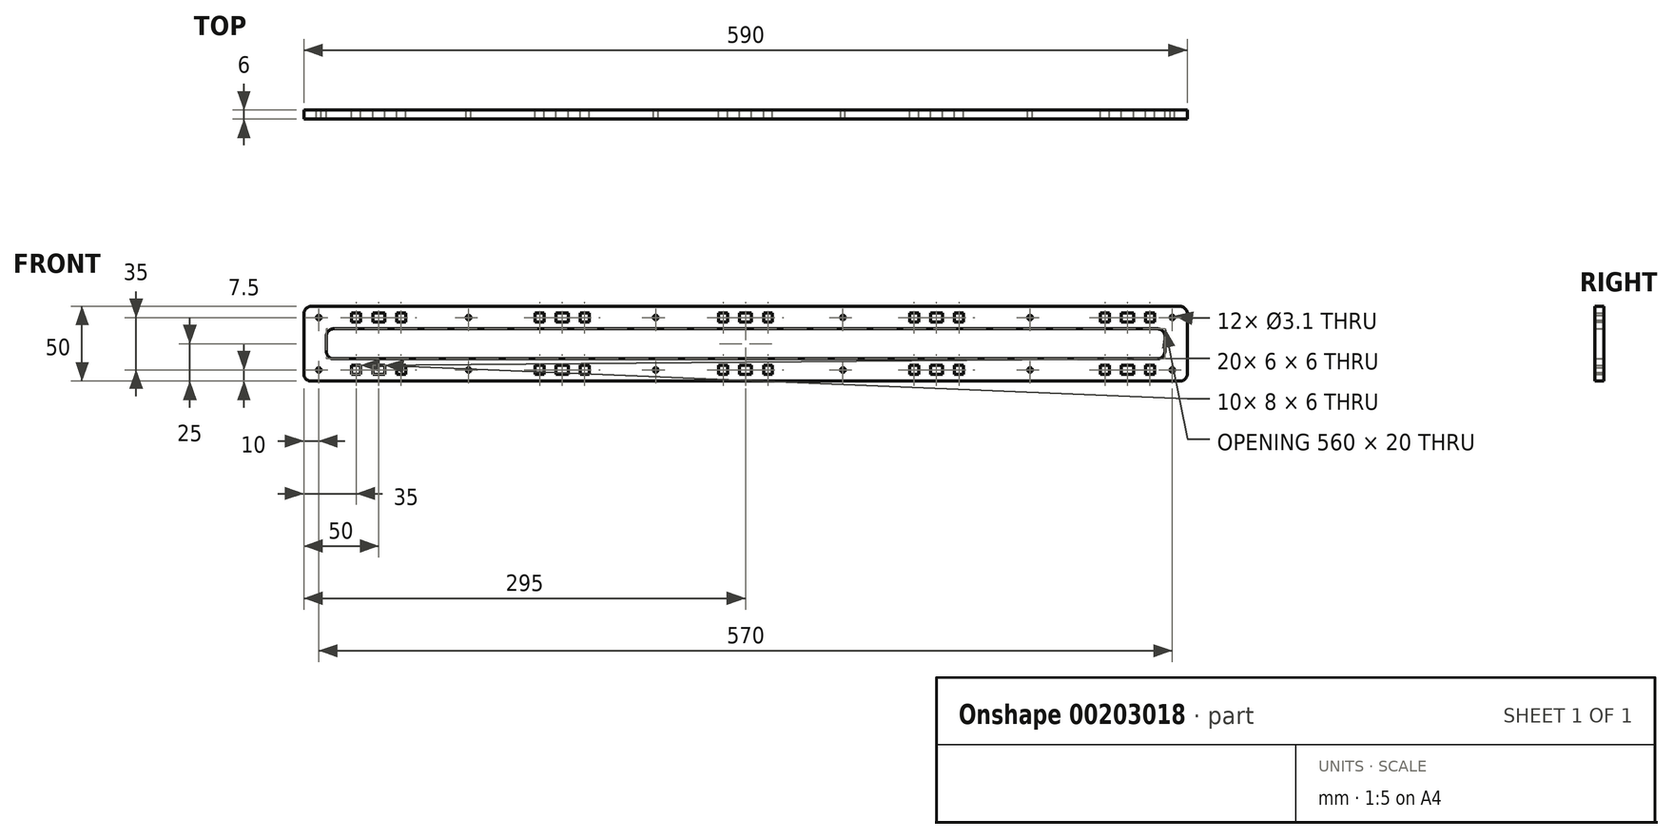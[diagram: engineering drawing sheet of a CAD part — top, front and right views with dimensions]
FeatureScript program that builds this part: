
annotation { "Feature Type Name" : "Feature", "Feature Type Description" : "" }
export const myFeature = defineFeature(function(context is Context, id is Id, definition is map)
    precondition{}
    {
        {
            var Q0;
            Q0=qCreatedBy(makeId("Front.planeOp"),FACE);
            var sketch = newSketch(context, id + "F0", { "sketchPlane" : qUnion([Q0])});
            skLineSegment(sketch, "E0", {"start": v(-290, 33.16) * mm, "end": v(290, 33.16) * mm});
            skArc(sketch, "E1", {"start": v(290, 33.16) * mm, "mid": v(293.54, 31.7) * mm, "end": v(295, 28.16) * mm});
            skLineSegment(sketch, "E2", {"start": v(295, 28.16) * mm, "end": v(295, -11.84) * mm});
            skArc(sketch, "E3", {"start": v(295, -11.84) * mm, "mid": v(293.54, -15.38) * mm, "end": v(290, -16.84) * mm});
            skLineSegment(sketch, "E4", {"start": v(290, -16.84) * mm, "end": v(-290, -16.84) * mm});
            skArc(sketch, "E5", {"start": v(-290, -16.84) * mm, "mid": v(-293.54, -15.38) * mm, "end": v(-295, -11.84) * mm});
            skLineSegment(sketch, "E6", {"start": v(-295, -11.84) * mm, "end": v(-295, 28.16) * mm});
            skArc(sketch, "E7", {"start": v(-295, 28.16) * mm, "mid": v(-293.54, 31.7) * mm, "end": v(-290, 33.16) * mm});
            skCircle(sketch, "E8", {"center": v(-285, -9.34) * mm, "radius": 1.55 * mm});
            skCircle(sketch, "E9", {"center": v(-285, 25.66) * mm, "radius": 1.55 * mm});
            skCircle(sketch, "E10", {"center": v(285, -9.34) * mm, "radius": 1.55 * mm});
            skCircle(sketch, "E11", {"center": v(285, 25.66) * mm, "radius": 1.55 * mm});
            skLineSegment(sketch, "E12", {"start": v(-275, 18.16) * mm, "end": v(275, 18.16) * mm});
            skArc(sketch, "E13", {"start": v(275, 18.16) * mm, "mid": v(278.54, 16.7) * mm, "end": v(280, 13.16) * mm});
            skLineSegment(sketch, "E14", {"start": v(280, 13.16) * mm, "end": v(280, 3.16) * mm});
            skArc(sketch, "E15", {"start": v(280, 3.16) * mm, "mid": v(278.54, -0.38) * mm, "end": v(275, -1.84) * mm});
            skLineSegment(sketch, "E16", {"start": v(275, -1.84) * mm, "end": v(-275, -1.84) * mm});
            skArc(sketch, "E17", {"start": v(-275, -1.84) * mm, "mid": v(-278.54, -0.38) * mm, "end": v(-280, 3.16) * mm});
            skLineSegment(sketch, "E18", {"start": v(-280, 3.16) * mm, "end": v(-280, 13.16) * mm});
            skArc(sketch, "E19", {"start": v(-280, 13.16) * mm, "mid": v(-278.54, 16.7) * mm, "end": v(-275, 18.16) * mm});
            skLineSegment(sketch, "E20", {"start": v(-249, 22.66) * mm, "end": v(-249, 28.66) * mm});
            skLineSegment(sketch, "E21", {"start": v(-249, 28.66) * mm, "end": v(-241, 28.66) * mm});
            skLineSegment(sketch, "E22", {"start": v(-241, 28.66) * mm, "end": v(-241, 22.66) * mm});
            skLineSegment(sketch, "E23", {"start": v(-241, 22.66) * mm, "end": v(-249, 22.66) * mm});
            skLineSegment(sketch, "E24", {"start": v(-233, 22.66) * mm, "end": v(-233, 28.66) * mm});
            skLineSegment(sketch, "E25", {"start": v(-233, 28.66) * mm, "end": v(-227, 28.66) * mm});
            skLineSegment(sketch, "E26", {"start": v(-227, 28.66) * mm, "end": v(-227, 22.66) * mm});
            skLineSegment(sketch, "E27", {"start": v(-227, 22.66) * mm, "end": v(-233, 22.66) * mm});
            skLineSegment(sketch, "E28", {"start": v(-257, 22.66) * mm, "end": v(-257, 28.66) * mm});
            skLineSegment(sketch, "E29", {"start": v(-257, 28.66) * mm, "end": v(-263, 28.66) * mm});
            skLineSegment(sketch, "E30", {"start": v(-263, 28.66) * mm, "end": v(-263, 22.66) * mm});
            skLineSegment(sketch, "E31", {"start": v(-263, 22.66) * mm, "end": v(-257, 22.66) * mm});
            skLineSegment(sketch, "E32", {"start": v(-126.5, 22.62) * mm, "end": v(-126.5, 28.62) * mm});
            skLineSegment(sketch, "E33", {"start": v(-126.5, 28.62) * mm, "end": v(-118.5, 28.62) * mm});
            skLineSegment(sketch, "E34", {"start": v(-118.5, 28.62) * mm, "end": v(-118.5, 22.62) * mm});
            skLineSegment(sketch, "E35", {"start": v(-118.5, 22.62) * mm, "end": v(-126.5, 22.62) * mm});
            skLineSegment(sketch, "E36", {"start": v(-110.5, 22.62) * mm, "end": v(-110.5, 28.62) * mm});
            skLineSegment(sketch, "E37", {"start": v(-110.5, 28.62) * mm, "end": v(-104.5, 28.62) * mm});
            skLineSegment(sketch, "E38", {"start": v(-104.5, 28.62) * mm, "end": v(-104.5, 22.62) * mm});
            skLineSegment(sketch, "E39", {"start": v(-104.5, 22.62) * mm, "end": v(-110.5, 22.62) * mm});
            skLineSegment(sketch, "E40", {"start": v(-134.5, 22.62) * mm, "end": v(-134.5, 28.62) * mm});
            skLineSegment(sketch, "E41", {"start": v(-134.5, 28.62) * mm, "end": v(-140.5, 28.62) * mm});
            skLineSegment(sketch, "E42", {"start": v(-140.5, 28.62) * mm, "end": v(-140.5, 22.62) * mm});
            skLineSegment(sketch, "E43", {"start": v(-140.5, 22.62) * mm, "end": v(-134.5, 22.62) * mm});
            skLineSegment(sketch, "E44", {"start": v(-4, 22.59) * mm, "end": v(-4, 28.59) * mm});
            skLineSegment(sketch, "E45", {"start": v(-4, 28.59) * mm, "end": v(4, 28.59) * mm});
            skLineSegment(sketch, "E46", {"start": v(4, 28.59) * mm, "end": v(4, 22.59) * mm});
            skLineSegment(sketch, "E47", {"start": v(4, 22.59) * mm, "end": v(-4, 22.59) * mm});
            skLineSegment(sketch, "E48", {"start": v(12, 22.59) * mm, "end": v(12, 28.59) * mm});
            skLineSegment(sketch, "E49", {"start": v(12, 28.59) * mm, "end": v(18, 28.59) * mm});
            skLineSegment(sketch, "E50", {"start": v(18, 28.59) * mm, "end": v(18, 22.59) * mm});
            skLineSegment(sketch, "E51", {"start": v(18, 22.59) * mm, "end": v(12, 22.59) * mm});
            skLineSegment(sketch, "E52", {"start": v(-12, 22.59) * mm, "end": v(-12, 28.59) * mm});
            skLineSegment(sketch, "E53", {"start": v(-12, 28.59) * mm, "end": v(-18, 28.59) * mm});
            skLineSegment(sketch, "E54", {"start": v(-18, 28.59) * mm, "end": v(-18, 22.59) * mm});
            skLineSegment(sketch, "E55", {"start": v(-18, 22.59) * mm, "end": v(-12, 22.59) * mm});
            skLineSegment(sketch, "E56", {"start": v(123.5, 22.62) * mm, "end": v(123.5, 28.62) * mm});
            skLineSegment(sketch, "E57", {"start": v(123.5, 28.62) * mm, "end": v(131.5, 28.62) * mm});
            skLineSegment(sketch, "E58", {"start": v(131.5, 28.62) * mm, "end": v(131.5, 22.62) * mm});
            skLineSegment(sketch, "E59", {"start": v(131.5, 22.62) * mm, "end": v(123.5, 22.62) * mm});
            skLineSegment(sketch, "E60", {"start": v(139.5, 22.62) * mm, "end": v(139.5, 28.62) * mm});
            skLineSegment(sketch, "E61", {"start": v(139.5, 28.62) * mm, "end": v(145.5, 28.62) * mm});
            skLineSegment(sketch, "E62", {"start": v(145.5, 28.62) * mm, "end": v(145.5, 22.62) * mm});
            skLineSegment(sketch, "E63", {"start": v(145.5, 22.62) * mm, "end": v(139.5, 22.62) * mm});
            skLineSegment(sketch, "E64", {"start": v(115.5, 22.62) * mm, "end": v(115.5, 28.62) * mm});
            skLineSegment(sketch, "E65", {"start": v(115.5, 28.62) * mm, "end": v(109.5, 28.62) * mm});
            skLineSegment(sketch, "E66", {"start": v(109.5, 28.62) * mm, "end": v(109.5, 22.62) * mm});
            skLineSegment(sketch, "E67", {"start": v(109.5, 22.62) * mm, "end": v(115.5, 22.62) * mm});
            skLineSegment(sketch, "E68", {"start": v(251, 22.66) * mm, "end": v(251, 28.66) * mm});
            skLineSegment(sketch, "E69", {"start": v(251, 28.66) * mm, "end": v(259, 28.66) * mm});
            skLineSegment(sketch, "E70", {"start": v(259, 28.66) * mm, "end": v(259, 22.66) * mm});
            skLineSegment(sketch, "E71", {"start": v(259, 22.66) * mm, "end": v(251, 22.66) * mm});
            skLineSegment(sketch, "E72", {"start": v(267, 22.66) * mm, "end": v(267, 28.66) * mm});
            skLineSegment(sketch, "E73", {"start": v(267, 28.66) * mm, "end": v(273, 28.66) * mm});
            skLineSegment(sketch, "E74", {"start": v(273, 28.66) * mm, "end": v(273, 22.66) * mm});
            skLineSegment(sketch, "E75", {"start": v(273, 22.66) * mm, "end": v(267, 22.66) * mm});
            skLineSegment(sketch, "E76", {"start": v(243, 22.66) * mm, "end": v(243, 28.66) * mm});
            skLineSegment(sketch, "E77", {"start": v(243, 28.66) * mm, "end": v(237, 28.66) * mm});
            skLineSegment(sketch, "E78", {"start": v(237, 28.66) * mm, "end": v(237, 22.66) * mm});
            skLineSegment(sketch, "E79", {"start": v(237, 22.66) * mm, "end": v(243, 22.66) * mm});
            skLineSegment(sketch, "E80", {"start": v(-249, -6.34) * mm, "end": v(-249, -12.34) * mm});
            skLineSegment(sketch, "E81", {"start": v(-249, -12.34) * mm, "end": v(-241, -12.34) * mm});
            skLineSegment(sketch, "E82", {"start": v(-241, -12.34) * mm, "end": v(-241, -6.34) * mm});
            skLineSegment(sketch, "E83", {"start": v(-241, -6.34) * mm, "end": v(-249, -6.34) * mm});
            skLineSegment(sketch, "E84", {"start": v(-233, -6.34) * mm, "end": v(-233, -12.34) * mm});
            skLineSegment(sketch, "E85", {"start": v(-233, -12.34) * mm, "end": v(-227, -12.34) * mm});
            skLineSegment(sketch, "E86", {"start": v(-227, -12.34) * mm, "end": v(-227, -6.34) * mm});
            skLineSegment(sketch, "E87", {"start": v(-227, -6.34) * mm, "end": v(-233, -6.34) * mm});
            skLineSegment(sketch, "E88", {"start": v(-257, -6.34) * mm, "end": v(-257, -12.34) * mm});
            skLineSegment(sketch, "E89", {"start": v(-257, -12.34) * mm, "end": v(-263, -12.34) * mm});
            skLineSegment(sketch, "E90", {"start": v(-263, -12.34) * mm, "end": v(-263, -6.34) * mm});
            skLineSegment(sketch, "E91", {"start": v(-263, -6.34) * mm, "end": v(-257, -6.34) * mm});
            skLineSegment(sketch, "E92", {"start": v(-126.5, -6.3) * mm, "end": v(-126.5, -12.3) * mm});
            skLineSegment(sketch, "E93", {"start": v(-126.5, -12.3) * mm, "end": v(-118.5, -12.3) * mm});
            skLineSegment(sketch, "E94", {"start": v(-118.5, -12.3) * mm, "end": v(-118.5, -6.3) * mm});
            skLineSegment(sketch, "E95", {"start": v(-118.5, -6.3) * mm, "end": v(-126.5, -6.3) * mm});
            skLineSegment(sketch, "E96", {"start": v(-110.5, -6.3) * mm, "end": v(-110.5, -12.3) * mm});
            skLineSegment(sketch, "E97", {"start": v(-110.5, -12.3) * mm, "end": v(-104.5, -12.3) * mm});
            skLineSegment(sketch, "E98", {"start": v(-104.5, -12.3) * mm, "end": v(-104.5, -6.3) * mm});
            skLineSegment(sketch, "E99", {"start": v(-104.5, -6.3) * mm, "end": v(-110.5, -6.3) * mm});
            skLineSegment(sketch, "E100", {"start": v(-134.5, -6.3) * mm, "end": v(-134.5, -12.3) * mm});
            skLineSegment(sketch, "E101", {"start": v(-134.5, -12.3) * mm, "end": v(-140.5, -12.3) * mm});
            skLineSegment(sketch, "E102", {"start": v(-140.5, -12.3) * mm, "end": v(-140.5, -6.3) * mm});
            skLineSegment(sketch, "E103", {"start": v(-140.5, -6.3) * mm, "end": v(-134.5, -6.3) * mm});
            skLineSegment(sketch, "E104", {"start": v(-4, -6.27) * mm, "end": v(-4, -12.27) * mm});
            skLineSegment(sketch, "E105", {"start": v(-4, -12.27) * mm, "end": v(4, -12.27) * mm});
            skLineSegment(sketch, "E106", {"start": v(4, -12.27) * mm, "end": v(4, -6.27) * mm});
            skLineSegment(sketch, "E107", {"start": v(4, -6.27) * mm, "end": v(-4, -6.27) * mm});
            skLineSegment(sketch, "E108", {"start": v(12, -6.27) * mm, "end": v(12, -12.27) * mm});
            skLineSegment(sketch, "E109", {"start": v(12, -12.27) * mm, "end": v(18, -12.27) * mm});
            skLineSegment(sketch, "E110", {"start": v(18, -12.27) * mm, "end": v(18, -6.27) * mm});
            skLineSegment(sketch, "E111", {"start": v(18, -6.27) * mm, "end": v(12, -6.27) * mm});
            skLineSegment(sketch, "E112", {"start": v(-12, -6.27) * mm, "end": v(-12, -12.27) * mm});
            skLineSegment(sketch, "E113", {"start": v(-12, -12.27) * mm, "end": v(-18, -12.27) * mm});
            skLineSegment(sketch, "E114", {"start": v(-18, -12.27) * mm, "end": v(-18, -6.27) * mm});
            skLineSegment(sketch, "E115", {"start": v(-18, -6.27) * mm, "end": v(-12, -6.27) * mm});
            skLineSegment(sketch, "E116", {"start": v(123.5, -6.3) * mm, "end": v(123.5, -12.3) * mm});
            skLineSegment(sketch, "E117", {"start": v(123.5, -12.3) * mm, "end": v(131.5, -12.3) * mm});
            skLineSegment(sketch, "E118", {"start": v(131.5, -12.3) * mm, "end": v(131.5, -6.3) * mm});
            skLineSegment(sketch, "E119", {"start": v(131.5, -6.3) * mm, "end": v(123.5, -6.3) * mm});
            skLineSegment(sketch, "E120", {"start": v(139.5, -6.3) * mm, "end": v(139.5, -12.3) * mm});
            skLineSegment(sketch, "E121", {"start": v(139.5, -12.3) * mm, "end": v(145.5, -12.3) * mm});
            skLineSegment(sketch, "E122", {"start": v(145.5, -12.3) * mm, "end": v(145.5, -6.3) * mm});
            skLineSegment(sketch, "E123", {"start": v(145.5, -6.3) * mm, "end": v(139.5, -6.3) * mm});
            skLineSegment(sketch, "E124", {"start": v(115.5, -6.3) * mm, "end": v(115.5, -12.3) * mm});
            skLineSegment(sketch, "E125", {"start": v(115.5, -12.3) * mm, "end": v(109.5, -12.3) * mm});
            skLineSegment(sketch, "E126", {"start": v(109.5, -12.3) * mm, "end": v(109.5, -6.3) * mm});
            skLineSegment(sketch, "E127", {"start": v(109.5, -6.3) * mm, "end": v(115.5, -6.3) * mm});
            skLineSegment(sketch, "E128", {"start": v(251, -6.34) * mm, "end": v(251, -12.34) * mm});
            skLineSegment(sketch, "E129", {"start": v(251, -12.34) * mm, "end": v(259, -12.34) * mm});
            skLineSegment(sketch, "E130", {"start": v(259, -12.34) * mm, "end": v(259, -6.34) * mm});
            skLineSegment(sketch, "E131", {"start": v(259, -6.34) * mm, "end": v(251, -6.34) * mm});
            skLineSegment(sketch, "E132", {"start": v(267, -6.34) * mm, "end": v(267, -12.34) * mm});
            skLineSegment(sketch, "E133", {"start": v(267, -12.34) * mm, "end": v(273, -12.34) * mm});
            skLineSegment(sketch, "E134", {"start": v(273, -12.34) * mm, "end": v(273, -6.34) * mm});
            skLineSegment(sketch, "E135", {"start": v(273, -6.34) * mm, "end": v(267, -6.34) * mm});
            skLineSegment(sketch, "E136", {"start": v(243, -6.34) * mm, "end": v(243, -12.34) * mm});
            skLineSegment(sketch, "E137", {"start": v(243, -12.34) * mm, "end": v(237, -12.34) * mm});
            skLineSegment(sketch, "E138", {"start": v(237, -12.34) * mm, "end": v(237, -6.34) * mm});
            skLineSegment(sketch, "E139", {"start": v(237, -6.34) * mm, "end": v(243, -6.34) * mm});
            skCircle(sketch, "E140", {"center": v(-185, -9.34) * mm, "radius": 1.55 * mm});
            skCircle(sketch, "E141", {"center": v(-185, 25.66) * mm, "radius": 1.55 * mm});
            skCircle(sketch, "E142", {"center": v(-60, -9.34) * mm, "radius": 1.55 * mm});
            skCircle(sketch, "E143", {"center": v(-60, 25.66) * mm, "radius": 1.55 * mm});
            skCircle(sketch, "E144", {"center": v(65, -9.34) * mm, "radius": 1.55 * mm});
            skCircle(sketch, "E145", {"center": v(65, 25.66) * mm, "radius": 1.55 * mm});
            skCircle(sketch, "E146", {"center": v(190, -9.34) * mm, "radius": 1.55 * mm});
            skCircle(sketch, "E147", {"center": v(190, 25.66) * mm, "radius": 1.55 * mm});
            skSolve(sketch);
        }
        {
            var Q0;
            Q0=makeQuery(id+"F0.imprint","IMPRINT",FACE,{"disambiguationData":[TD([[makeQuery(id+"F0.imprint","IMPRINT",EDGE,{"derivedFrom":sQuery(id+"F0.wireOp",EDGE,"E0")}),-1.0]])]});
            extrude(context, id + "F1", {"entities" : qUnion([Q0]), "depth" : 6 * mm});
        }
    });
